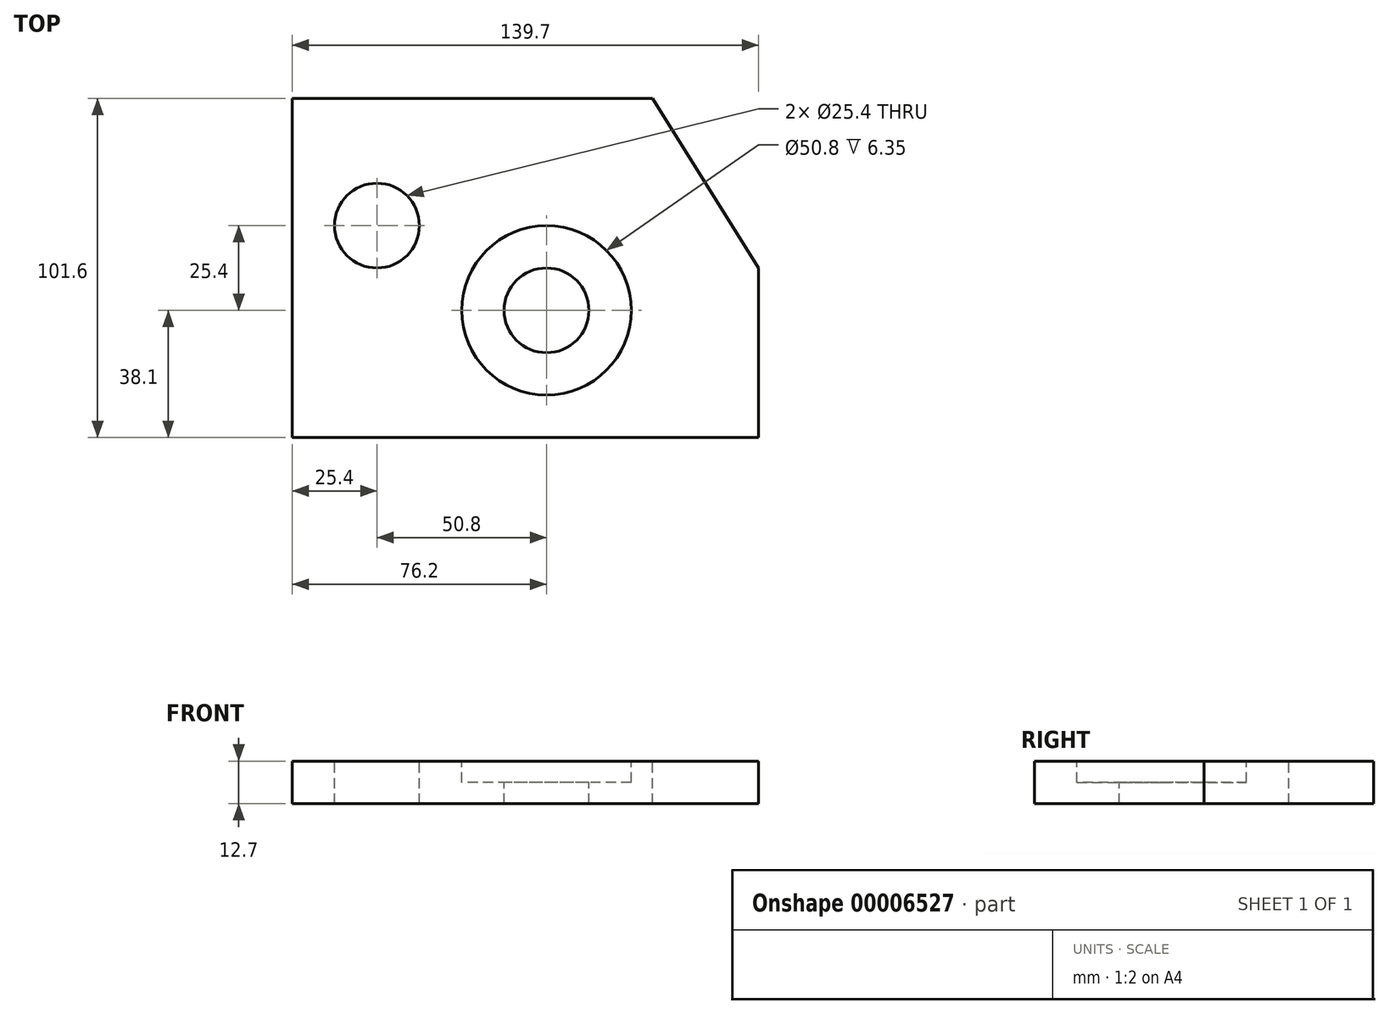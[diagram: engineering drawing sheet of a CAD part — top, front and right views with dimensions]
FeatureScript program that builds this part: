
annotation { "Feature Type Name" : "Feature", "Feature Type Description" : "" }
export const myFeature = defineFeature(function(context is Context, id is Id, definition is map)
    precondition{}
    {
        {
            var Q0;
            Q0=qCreatedBy(makeId("Top.planeOp"),FACE);
            var sketch = newSketch(context, id + "F0", { "sketchPlane" : qUnion([Q0])});
            skLineSegment(sketch, "E0.bottom", {"start": v(0, 0) * mm, "end": v(139.7, 0) * mm});
            skLineSegment(sketch, "E0.top", {"start": v(0, 101.6) * mm, "end": v(107.95, 101.6) * mm});
            skLineSegment(sketch, "E0.left", {"start": v(0, 0) * mm, "end": v(0, 101.6) * mm});
            skLineSegment(sketch, "E0.right", {"start": v(139.7, 0) * mm, "end": v(139.7, 50.8) * mm});
            skLineSegment(sketch, "E1", {"start": v(107.95, 101.6) * mm, "end": v(139.7, 50.8) * mm});
            skCircle(sketch, "E2", {"center": v(25.4, 63.5) * mm, "radius": 12.7 * mm});
            skCircle(sketch, "E3", {"center": v(76.2, 38.1) * mm, "radius": 12.7 * mm});
            skCircle(sketch, "E4", {"center": v(76.2, 38.1) * mm, "radius": 25.4 * mm});
            skSolve(sketch);
        }
        {
            var Q0;
            Q0=makeQuery(id+"F0.imprint","IMPRINT",FACE,{"disambiguationData":[TD([[makeQuery(id+"F0.imprint","IMPRINT",EDGE,{"derivedFrom":sQuery(id+"F0.wireOp",EDGE,"E0.bottom")}),1.0]])]});
            var Q1;
            Q1=makeQuery(id+"F0.imprint","IMPRINT",FACE,{"disambiguationData":[TD([[makeQuery(id+"F0.imprint","IMPRINT",EDGE,{"derivedFrom":sQuery(id+"F0.wireOp",EDGE,"E3")}),-1.0]])]});
            extrude(context, id + "F1", {"entities" : qUnion([Q0, Q1]), "oppositeDirection" : true, "depth" : 12.7 * mm});
        }
        {
            var Q0;
            Q0=makeQuery(id+"F0.imprint","IMPRINT",FACE,{"disambiguationData":[TD([[makeQuery(id+"F0.imprint","IMPRINT",EDGE,{"derivedFrom":sQuery(id+"F0.wireOp",EDGE,"E3")}),-1.0]])]});
            extrude(context, id + "F2", {"entities" : qUnion([Q0]), "operationType" : NewBodyOperationType.REMOVE, "oppositeDirection" : true, "depth" : 6.35 * mm});
        }
    });
